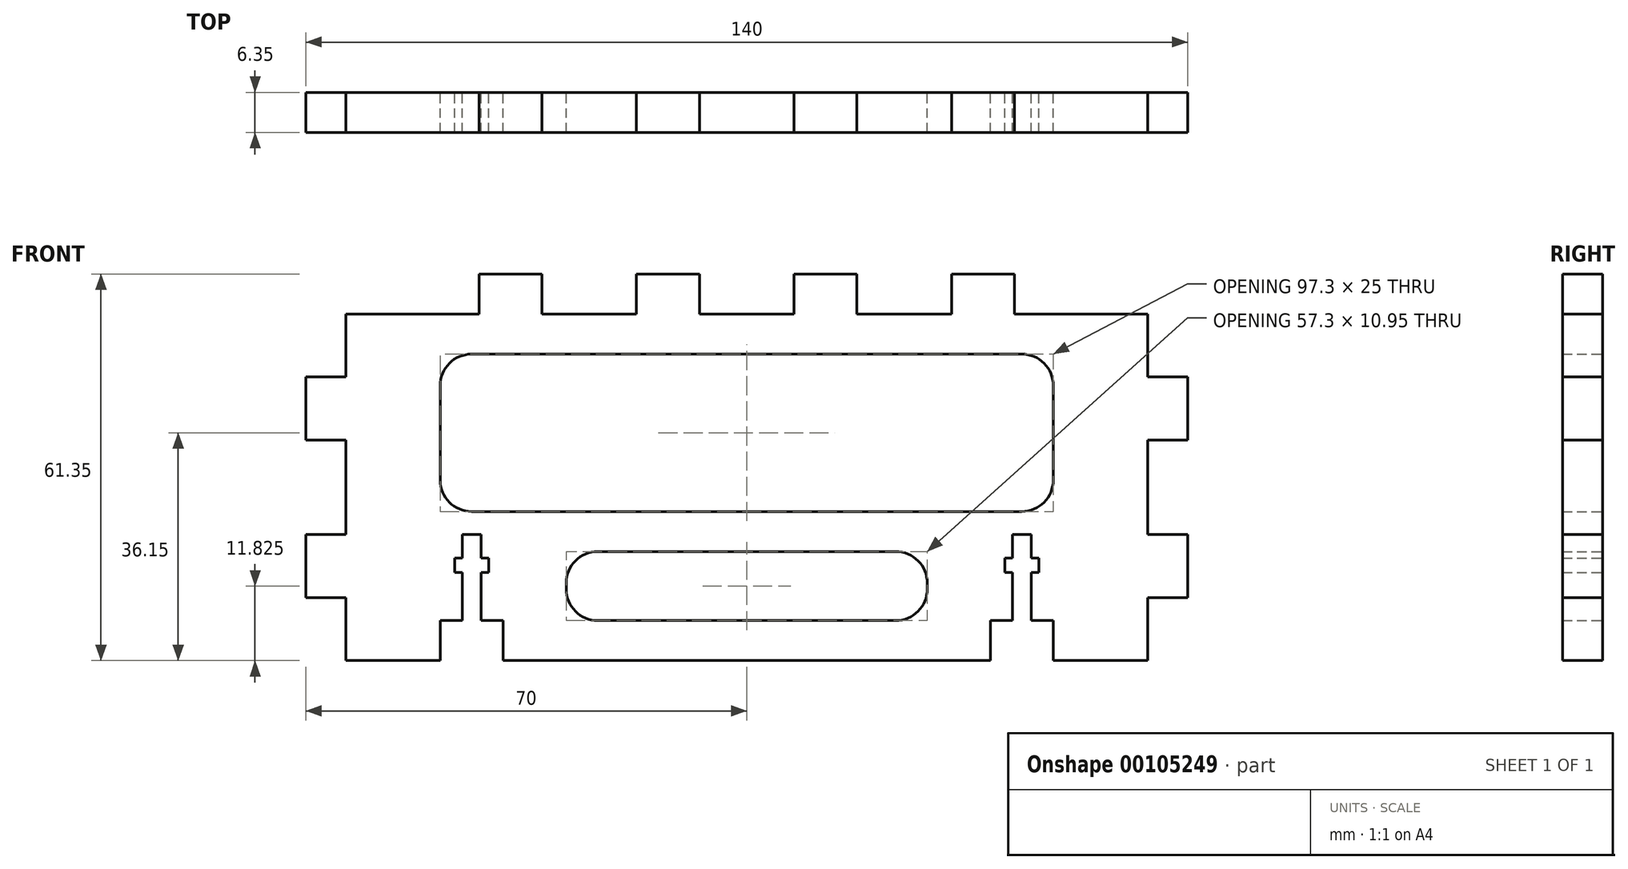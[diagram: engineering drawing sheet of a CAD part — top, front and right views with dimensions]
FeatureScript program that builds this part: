
annotation { "Feature Type Name" : "Feature", "Feature Type Description" : "" }
export const myFeature = defineFeature(function(context is Context, id is Id, definition is map)
    precondition{}
    {
        {
            var Q0;
            Q0=qCreatedBy(makeId("Front.planeOp"),FACE);
            var sketch = newSketch(context, id + "F0", { "sketchPlane" : qUnion([Q0])});
            skLineSegment(sketch, "E0.bottom", {"start": v(0, 0) * mm, "end": v(15, 0) * mm});
            skLineSegment(sketch, "E0.top", {"start": v(0, 55) * mm, "end": v(21.15, 55) * mm});
            skLineSegment(sketch, "E0.left", {"start": v(0, 0) * mm, "end": v(0, 10) * mm});
            skLineSegment(sketch, "E0.right", {"start": v(127.3, 0) * mm, "end": v(127.3, 10) * mm});
            skLineSegment(sketch, "E1.top", {"start": v(21.15, 61.35) * mm, "end": v(31.15, 61.35) * mm});
            skLineSegment(sketch, "E1.left", {"start": v(21.15, 55) * mm, "end": v(21.15, 61.35) * mm});
            skLineSegment(sketch, "E1.right", {"start": v(31.15, 55) * mm, "end": v(31.15, 61.35) * mm});
            skLineSegment(sketch, "E2.trimOffspring", {"start": v(31.15, 55) * mm, "end": v(46.15, 55) * mm});
            skLineSegment(sketch, "E3.1.0.0", {"start": v(46.15, 61.35) * mm, "end": v(56.15, 61.35) * mm});
            skLineSegment(sketch, "E3.1.0.1", {"start": v(46.15, 55) * mm, "end": v(46.15, 61.35) * mm});
            skLineSegment(sketch, "E3.1.0.2", {"start": v(56.15, 55) * mm, "end": v(56.15, 61.35) * mm});
            skLineSegment(sketch, "E3.2.0.0", {"start": v(71.15, 61.35) * mm, "end": v(81.15, 61.35) * mm});
            skLineSegment(sketch, "E3.2.0.1", {"start": v(71.15, 55) * mm, "end": v(71.15, 61.35) * mm});
            skLineSegment(sketch, "E3.2.0.2", {"start": v(81.15, 55) * mm, "end": v(81.15, 61.35) * mm});
            skLineSegment(sketch, "E3.3.0.0", {"start": v(96.15, 61.35) * mm, "end": v(106.15, 61.35) * mm});
            skLineSegment(sketch, "E3.3.0.1", {"start": v(96.15, 55) * mm, "end": v(96.15, 61.35) * mm});
            skLineSegment(sketch, "E3.3.0.2", {"start": v(106.15, 55) * mm, "end": v(106.15, 61.35) * mm});
            skLineSegment(sketch, "E3.direction1", {"start": v(21.15, 55) * mm, "end": v(46.15, 55) * mm, "construction": true});
            skLineSegment(sketch, "E4.trimOffspring", {"start": v(56.15, 55) * mm, "end": v(71.15, 55) * mm});
            skLineSegment(sketch, "E5.trimOffspring", {"start": v(81.15, 55) * mm, "end": v(96.15, 55) * mm});
            skLineSegment(sketch, "E6.trimOffspring", {"start": v(106.15, 55) * mm, "end": v(127.3, 55) * mm});
            skLineSegment(sketch, "E7.bottom", {"start": v(0, 45) * mm, "end": v(-6.35, 45) * mm});
            skLineSegment(sketch, "E7.top", {"start": v(0, 35) * mm, "end": v(-6.35, 35) * mm});
            skLineSegment(sketch, "E7.right", {"start": v(-6.35, 45) * mm, "end": v(-6.35, 35) * mm});
            skLineSegment(sketch, "E8.bottom", {"start": v(0, 20) * mm, "end": v(-6.35, 20) * mm});
            skLineSegment(sketch, "E8.top", {"start": v(0, 10) * mm, "end": v(-6.35, 10) * mm});
            skLineSegment(sketch, "E8.right", {"start": v(-6.35, 20) * mm, "end": v(-6.35, 10) * mm});
            skLineSegment(sketch, "E9.bottom", {"start": v(127.3, 45) * mm, "end": v(133.65, 45) * mm});
            skLineSegment(sketch, "E9.top", {"start": v(127.3, 35) * mm, "end": v(133.65, 35) * mm});
            skLineSegment(sketch, "E9.right", {"start": v(133.65, 45) * mm, "end": v(133.65, 35) * mm});
            skLineSegment(sketch, "E10.bottom", {"start": v(127.3, 20) * mm, "end": v(133.65, 20) * mm});
            skLineSegment(sketch, "E10.top", {"start": v(127.3, 10) * mm, "end": v(133.65, 10) * mm});
            skLineSegment(sketch, "E10.right", {"start": v(133.65, 20) * mm, "end": v(133.65, 10) * mm});
            skLineSegment(sketch, "E11.trimOffspring", {"start": v(0, 45) * mm, "end": v(0, 55) * mm});
            skLineSegment(sketch, "E12.trimOffspring", {"start": v(0, 20) * mm, "end": v(0, 35) * mm});
            skLineSegment(sketch, "E13.trimOffspring", {"start": v(25, 0) * mm, "end": v(102.3, 0) * mm});
            skLineSegment(sketch, "E14.trimOffspring", {"start": v(112.3, 0) * mm, "end": v(127.3, 0) * mm});
            skLineSegment(sketch, "E15.trimOffspring", {"start": v(127.3, 20) * mm, "end": v(127.3, 35) * mm});
            skLineSegment(sketch, "E16.trimOffspring", {"start": v(127.3, 45) * mm, "end": v(127.3, 55) * mm});
            skLineSegment(sketch, "E17.MirrorCS", {"start": v(21.5, 6.35) * mm, "end": v(21.5, 14) * mm});
            skLineSegment(sketch, "E18.MirrorCS", {"start": v(18.5, 20) * mm, "end": v(21.5, 20) * mm});
            skLineSegment(sketch, "E19.MirrorCS", {"start": v(18.5, 6.35) * mm, "end": v(18.5, 14) * mm});
            skLineSegment(sketch, "E20.bottom", {"start": v(17.3, 16.27) * mm, "end": v(18.5, 16.27) * mm});
            skLineSegment(sketch, "E20.top", {"start": v(17.3, 14) * mm, "end": v(18.5, 14) * mm});
            skLineSegment(sketch, "E20.left", {"start": v(17.3, 16.27) * mm, "end": v(17.3, 14) * mm});
            skLineSegment(sketch, "E20.right", {"start": v(22.7, 16.27) * mm, "end": v(22.7, 14) * mm});
            skLineSegment(sketch, "E21.trimOffspring", {"start": v(21.5, 16.27) * mm, "end": v(22.7, 16.27) * mm});
            skLineSegment(sketch, "E22.trimOffspring", {"start": v(21.5, 14) * mm, "end": v(22.7, 14) * mm});
            skLineSegment(sketch, "E23.trimOffspring", {"start": v(18.5, 16.27) * mm, "end": v(18.5, 20) * mm});
            skLineSegment(sketch, "E24.trimOffspring", {"start": v(21.5, 16.27) * mm, "end": v(21.5, 20) * mm});
            skLineSegment(sketch, "E25.top", {"start": v(21.5, 6.35) * mm, "end": v(25, 6.35) * mm});
            skLineSegment(sketch, "E25.right", {"start": v(25, 0) * mm, "end": v(25, 6.35) * mm});
            skPoint(sketch, "E26.oppositeSnap0", {"position": v(23.25, 6.35) * mm});
            skLineSegment(sketch, "E26.top", {"start": v(18.5, 6.35) * mm, "end": v(15, 6.35) * mm});
            skLineSegment(sketch, "E26.right", {"start": v(15, 0) * mm, "end": v(15, 6.35) * mm});
            skPoint(sketch, "E27.orphan", {"position": v(21.5, 0) * mm});
            skPoint(sketch, "E26.bottom.start.orphan", {"position": v(18.5, 0) * mm});
            skLineSegment(sketch, "E28", {"start": v(63.65, 55) * mm, "end": v(63.65, 0) * mm, "construction": true});
            skPoint(sketch, "E28.endSnap0", {"position": v(63.65, 0) * mm});
            skLineSegment(sketch, "E29.MirrorCS", {"start": v(105.8, 6.35) * mm, "end": v(102.3, 6.35) * mm});
            skLineSegment(sketch, "E30.MirrorCS", {"start": v(104.6, 16.27) * mm, "end": v(104.6, 14) * mm});
            skLineSegment(sketch, "E31.MirrorCS", {"start": v(105.8, 16.27) * mm, "end": v(105.8, 20) * mm});
            skLineSegment(sketch, "E32.MirrorCS", {"start": v(110, 14) * mm, "end": v(108.8, 14) * mm});
            skLineSegment(sketch, "E33.MirrorCS", {"start": v(112.3, 0) * mm, "end": v(112.3, 6.35) * mm});
            skLineSegment(sketch, "E34.MirrorCS", {"start": v(105.8, 6.35) * mm, "end": v(105.8, 14) * mm});
            skLineSegment(sketch, "E35.MirrorCS", {"start": v(110, 16.27) * mm, "end": v(108.8, 16.27) * mm});
            skLineSegment(sketch, "E36.MirrorCS", {"start": v(105.8, 16.27) * mm, "end": v(104.6, 16.27) * mm});
            skLineSegment(sketch, "E37.MirrorCS", {"start": v(108.8, 20) * mm, "end": v(105.8, 20) * mm});
            skLineSegment(sketch, "E38.MirrorCS", {"start": v(110, 16.27) * mm, "end": v(110, 14) * mm});
            skLineSegment(sketch, "E39.MirrorCS", {"start": v(108.8, 16.27) * mm, "end": v(108.8, 20) * mm});
            skLineSegment(sketch, "E40.MirrorCS", {"start": v(102.3, 0) * mm, "end": v(102.3, 6.35) * mm});
            skPoint(sketch, "E41.MirrorP", {"position": v(104.05, 6.35) * mm});
            skLineSegment(sketch, "E42.MirrorCS", {"start": v(105.8, 14) * mm, "end": v(104.6, 14) * mm});
            skLineSegment(sketch, "E43.MirrorCS", {"start": v(108.8, 6.35) * mm, "end": v(108.8, 14) * mm});
            skLineSegment(sketch, "E44.MirrorCS", {"start": v(108.8, 6.35) * mm, "end": v(112.3, 6.35) * mm});
            skLineSegment(sketch, "E45.bottom", {"start": v(20, 48.65) * mm, "end": v(107.3, 48.65) * mm});
            skLineSegment(sketch, "E45.top", {"start": v(20, 23.65) * mm, "end": v(107.3, 23.65) * mm});
            skLineSegment(sketch, "E45.left", {"start": v(15, 43.65) * mm, "end": v(15, 28.65) * mm});
            skLineSegment(sketch, "E45.right", {"start": v(112.3, 43.65) * mm, "end": v(112.3, 28.65) * mm});
            skLineSegment(sketch, "E46.bottom", {"start": v(40, 17.3) * mm, "end": v(87.3, 17.3) * mm});
            skLineSegment(sketch, "E46.top", {"start": v(40, 6.35) * mm, "end": v(87.3, 6.35) * mm});
            skLineSegment(sketch, "E46.left", {"start": v(35, 12.3) * mm, "end": v(35, 11.35) * mm});
            skLineSegment(sketch, "E46.right", {"start": v(92.3, 12.3) * mm, "end": v(92.3, 11.35) * mm});
            skPoint(sketch, "E47.visualSharp", {"position": v(15, 48.65) * mm});
            skArc(sketch, "E47.filletArc", {"start": v(20, 48.65) * mm, "mid": v(16.46, 47.19) * mm, "end": v(15, 43.65) * mm});
            skPoint(sketch, "E48.visualSharp", {"position": v(15, 23.65) * mm});
            skArc(sketch, "E48.filletArc", {"start": v(15, 28.65) * mm, "mid": v(16.46, 25.11) * mm, "end": v(20, 23.65) * mm});
            skPoint(sketch, "E49.visualSharp", {"position": v(112.3, 23.65) * mm});
            skArc(sketch, "E49.filletArc", {"start": v(107.3, 23.65) * mm, "mid": v(110.84, 25.11) * mm, "end": v(112.3, 28.65) * mm});
            skPoint(sketch, "E50.visualSharp", {"position": v(112.3, 48.65) * mm});
            skArc(sketch, "E50.filletArc", {"start": v(112.3, 43.65) * mm, "mid": v(110.84, 47.19) * mm, "end": v(107.3, 48.65) * mm});
            skPoint(sketch, "E51.visualSharp", {"position": v(35, 17.3) * mm});
            skArc(sketch, "E51.filletArc", {"start": v(40, 17.3) * mm, "mid": v(36.46, 15.84) * mm, "end": v(35, 12.3) * mm});
            skPoint(sketch, "E52.visualSharp", {"position": v(35, 6.35) * mm});
            skArc(sketch, "E52.filletArc", {"start": v(35, 11.35) * mm, "mid": v(36.46, 7.81) * mm, "end": v(40, 6.35) * mm});
            skPoint(sketch, "E53.visualSharp", {"position": v(92.3, 6.35) * mm});
            skArc(sketch, "E53.filletArc", {"start": v(87.3, 6.35) * mm, "mid": v(90.84, 7.81) * mm, "end": v(92.3, 11.35) * mm});
            skPoint(sketch, "E54.visualSharp", {"position": v(92.3, 17.3) * mm});
            skArc(sketch, "E54.filletArc", {"start": v(92.3, 12.3) * mm, "mid": v(90.84, 15.84) * mm, "end": v(87.3, 17.3) * mm});
            skSolve(sketch);
        }
        {
            var Q0;
            Q0 = qSketchRegion(id + "F0", true);
            extrude(context, id + "F1", {"entities" : qUnion([Q0]), "depth" : 6.35 * mm});
        }
    });
